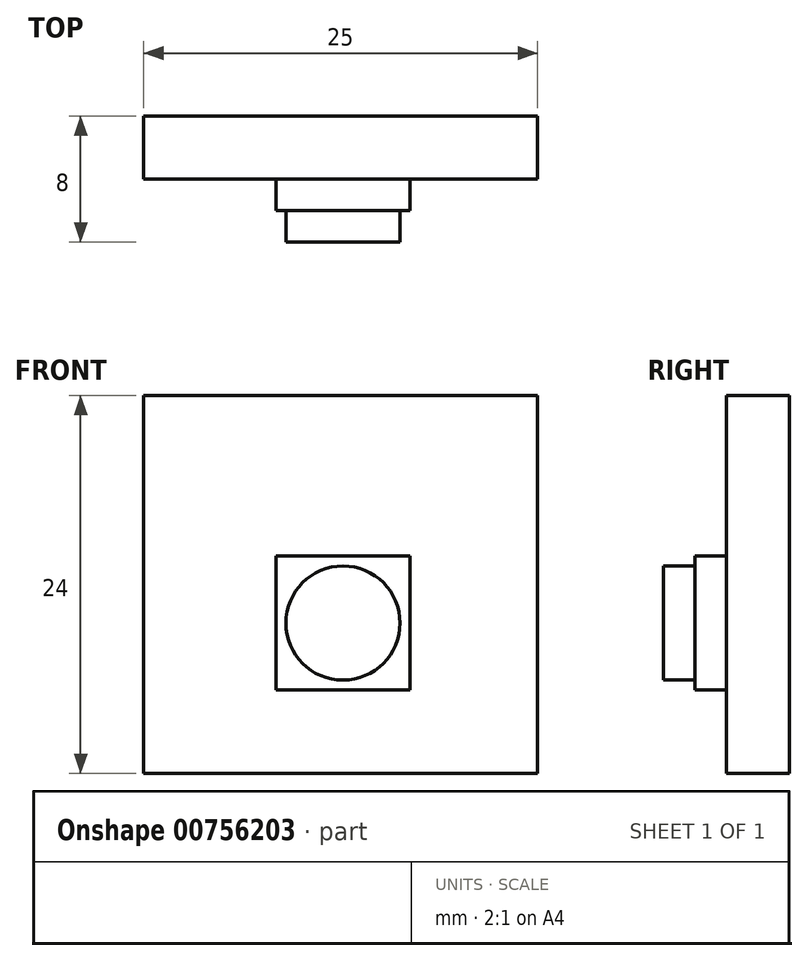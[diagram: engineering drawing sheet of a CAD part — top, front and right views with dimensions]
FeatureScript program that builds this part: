
annotation { "Feature Type Name" : "Feature", "Feature Type Description" : "" }
export const myFeature = defineFeature(function(context is Context, id is Id, definition is map)
    precondition{}
    {
        {
            var Q0;
            Q0=qCreatedBy(makeId("Front.planeOp"),FACE);
            var sketch = newSketch(context, id + "F0", { "sketchPlane" : qUnion([Q0])});
            skLineSegment(sketch, "E0.bottom", {"start": v(-12.5, 12) * mm, "end": v(12.5, 12) * mm});
            skLineSegment(sketch, "E0.top", {"start": v(-12.5, -12) * mm, "end": v(12.5, -12) * mm});
            skLineSegment(sketch, "E0.left", {"start": v(-12.5, 12) * mm, "end": v(-12.5, -12) * mm});
            skLineSegment(sketch, "E0.right", {"start": v(12.5, 12) * mm, "end": v(12.5, -12) * mm});
            skPoint(sketch, "E0.middle", {"position": v(0, 0) * mm});
            skSolve(sketch);
        }
        {
            var Q0;
            Q0 = qSketchRegion(id + "F0", true);
            extrude(context, id + "F1", {"entities" : qUnion([Q0]), "endBound" : BoundingType.SYMMETRIC, "depth" : 4 * mm, "offsetDistance" : 25 * mm});
        }
        {
            var Q0;
            Q0=makeQuery(id+"F1.opExtrude","CAP_FACE",FACE,{"disambiguationData":[OSD([sQuery(id+"F0.wireOp",EDGE,"E0.bottom"),sQuery(id+"F0.wireOp",EDGE,"E0.top"),sQuery(id+"F0.wireOp",EDGE,"E0.left"),sQuery(id+"F0.wireOp",EDGE,"E0.right")])],"isStart":false});
            var sketch = newSketch(context, id + "F2", { "sketchPlane" : qUnion([Q0])});
            skLineSegment(sketch, "E1.bottom", {"start": v(4.4, 1.8) * mm, "end": v(-4.1, 1.8) * mm});
            skLineSegment(sketch, "E1.top", {"start": v(4.4, -6.7) * mm, "end": v(-4.1, -6.7) * mm});
            skLineSegment(sketch, "E1.left", {"start": v(4.4, 1.8) * mm, "end": v(4.4, -6.7) * mm});
            skLineSegment(sketch, "E1.right", {"start": v(-4.1, 1.8) * mm, "end": v(-4.1, -6.7) * mm});
            skPoint(sketch, "E1.middle", {"position": v(0.15, -2.45) * mm});
            skSolve(sketch);
        }
        {
            var Q0;
            Q0 = qSketchRegion(id + "F2", true);
            extrude(context, id + "F3", {"entities" : qUnion([Q0]), "operationType" : NewBodyOperationType.ADD, "depth" : 2 * mm, "offsetDistance" : 25 * mm});
        }
        {
            var Q0;
            Q0=makeQuery(id+"F3.opExtrude","CAP_FACE",FACE,{"disambiguationData":[OSD([sQuery(id+"F2.wireOp",EDGE,"E1.bottom"),sQuery(id+"F2.wireOp",EDGE,"E1.top"),sQuery(id+"F2.wireOp",EDGE,"E1.left"),sQuery(id+"F2.wireOp",EDGE,"E1.right")])],"isStart":false});
            var sketch = newSketch(context, id + "F4", { "sketchPlane" : qUnion([Q0])});
            skLineSegment(sketch, "E2", {"start": v(0.15, 1.8) * mm, "end": v(0.15, -6.7) * mm, "construction": true});
            skCircle(sketch, "E3", {"center": v(0.15, -2.45) * mm, "radius": 3.62 * mm});
            skSolve(sketch);
        }
        {
            var Q0;
            Q0 = qSketchRegion(id + "F4", true);
            extrude(context, id + "F5", {"entities" : qUnion([Q0]), "operationType" : NewBodyOperationType.ADD, "depth" : 2 * mm, "offsetDistance" : 25 * mm});
        }
    });
